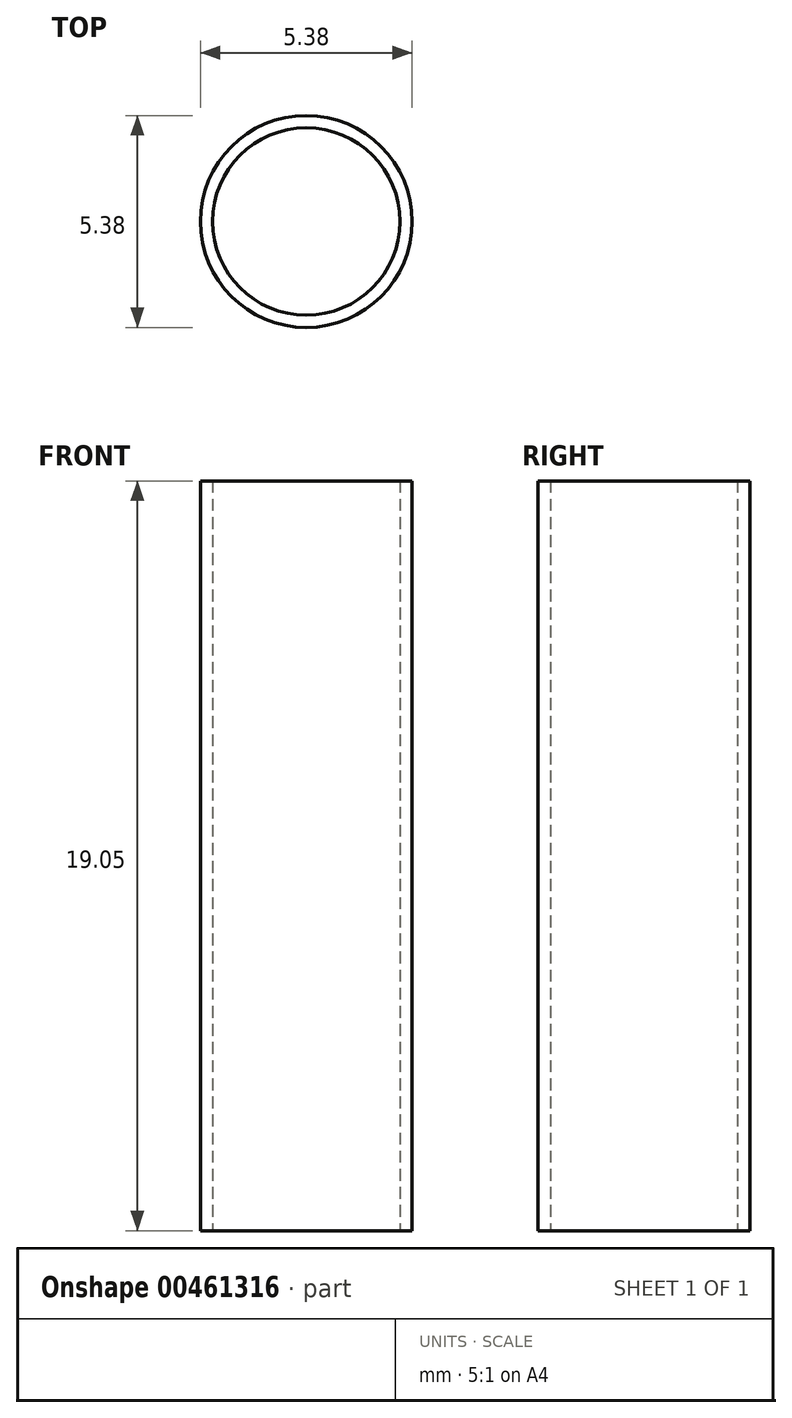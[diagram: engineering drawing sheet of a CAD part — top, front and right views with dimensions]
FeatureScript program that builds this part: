
annotation { "Feature Type Name" : "Feature", "Feature Type Description" : "" }
export const myFeature = defineFeature(function(context is Context, id is Id, definition is map)
    precondition{}
    {
        {
            var Q0;
            Q0=qCreatedBy(makeId("Top.planeOp"),FACE);
            var sketch = newSketch(context, id + "F0", { "sketchPlane" : qUnion([Q0])});
            skCircle(sketch, "E0", {"center": v(0, 0) * mm, "radius": 2.38 * mm});
            skCircle(sketch, "E1.0", {"center": v(0, 0) * mm, "radius": 3.02 * mm});
            skLineSegment(sketch, "E2", {"start": v(-1.48, 2.63) * mm, "end": v(-1.17, 2.07) * mm});
            skCircle(sketch, "E3", {"center": v(0, 0) * mm, "radius": 2.7 * mm});
            skSolve(sketch);
        }
        {
            var Q0;
            Q0=makeQuery(id+"F0.imprint","IMPRINT",FACE,{"disambiguationData":[TD([[makeQuery(id+"F0.imprint","IMPRINT",EDGE,{"derivedFrom":sQuery(id+"F0.wireOp",EDGE,"E0")}),-1.0]])]});
            extrude(context, id + "F1", {"entities" : qUnion([Q0]), "depth" : 19.05 * mm});
        }
    });
